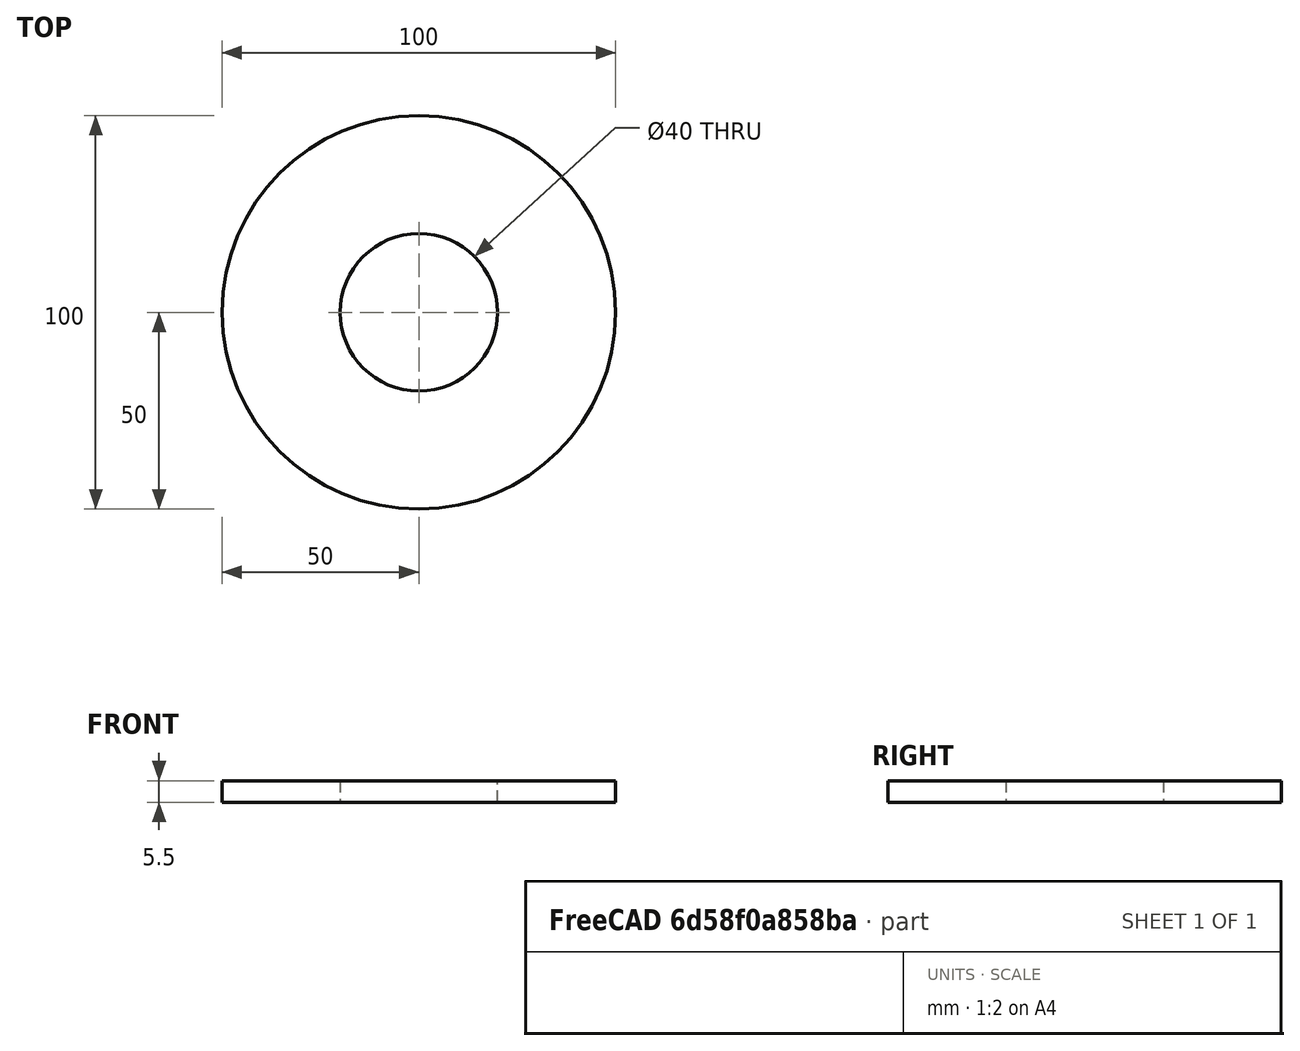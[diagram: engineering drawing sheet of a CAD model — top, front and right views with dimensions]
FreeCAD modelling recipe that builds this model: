
FCSTD DOCUMENT  (FreeCAD 0.19R24276 (Git))
Label: rubber
License: All rights reserved
LicenseURL: http://en.wikipedia.org/wiki/All_rights_reserved
objects: Sketcher::SketchObject×1, PartDesign::Pad×1, PartDesign::Body×1
note: 4 computed .brp shape members not serialized (recipe doc carries the construction recipe); baked Part::Feature solids carry a one-line shape summary decoded from their .brp

FEATURE [Sketcher::SketchObject] Sketch
  FullyConstrained = true
  MapMode = 5
  Support = -> [XY_Plane]
  sketch-geometry (2):
    g0: Circle CenterX=0 CenterY=0 CenterZ=0 NormalX=0 NormalY=0 NormalZ=1 AngleXU=0 Radius=50
    g1: Circle CenterX=0 CenterY=0 CenterZ=0 NormalX=0 NormalY=0 NormalZ=1 AngleXU=0 Radius=20
  constraints (4):
    c: Coincident(g0,g-1)
    c: Coincident(g1,g0)
    c: Diameter(g1) = 40
    c: Diameter(g0) = 100
FEATURE [PartDesign::Pad] Pad
  Direction = (1,1,1)
  Length = 5.5
  Length2 = 100
  Profile = -> Sketch
  Type = 0
FEATURE [PartDesign::Body] Body
  Group = -> [Sketch,Pad]
  Origin = -> Origin
  Tip = -> Pad
